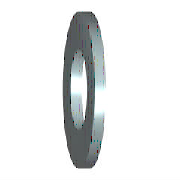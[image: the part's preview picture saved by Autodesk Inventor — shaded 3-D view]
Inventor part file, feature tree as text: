
AUTODESK INVENTOR PART (.ipt)
format: ipt  version: 2015 (Build 190159000, 159)  size: 109,056 bytes
history: native  units: mm (DEFAULTED — no unit token found)
features: other x1, plane x1, sketch x1
ambient origin geometry x7: Origin, YZ Plane, XY Plane, X Axis, Y Axis, Z Axis, Center Point
bodies: Solid1 (feature_tree), Body (feature_tree)
feature tree (3):
  other  "Work Axis1"
  plane  "Work Plane1"
  sketch  "Sketch"  dims[d0=3.2mm d1=7.0mm d2=0.5mm d3=0.0mm d4=0.0mm d5=0.0mm d6=0.0mm d7=0.0mm]
